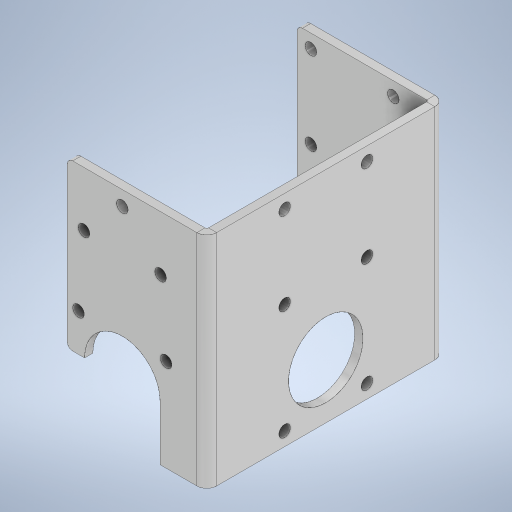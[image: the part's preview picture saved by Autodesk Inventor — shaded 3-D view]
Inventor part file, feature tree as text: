
AUTODESK INVENTOR PART (.ipt)
format: ipt  version: 2024.2 (Build 282272000, 272)  size: 324,096 bytes
history: native  units: in
note: dims shown in document units (in); Inventor stores cm internally (conversion verified against a paired STEP export)
features: reference x11, sketch x8, other x7, sheet_metal_op x4, hole x3, plane x1, chamfer x1, extrude x1
ambient origin geometry x8: Origin, YZ Plane, XZ Plane, XY Plane, X Axis, Y Axis, Z Axis, Center Point
bodies: Solid1 (feature_tree)
feature tree (36):
  sheet_metal_op  "Face1"
  sheet_metal_op  "Flange1"
  sketch  "Sketch3"  dims[d4=0.0295in d5=0.1181in]
  sketch  "Sketch4"  dims[d6=0.0122in d7=1.0039in d8=90.0deg d9=0.0122in]
  plane  "Work Plane1"
  hole  "Hole1"  [1 undecoded]
  sketch  "Sketch6"  dims[d11=0.0591in]
  chamfer  "Corner Round1"
  hole  "Hole3"  [1 undecoded]
  hole  "Hole4"  [1 undecoded]
  extrude  "Extrusion1"  Depth=1.0039in TaperAngle=90.0deg
  sketch  "Sketch1"  dims[d0=1.5787in d1=1.5945in]
  other  "Plate1"
  sketch  "Sketch2"  dims[d2=0.0591in d3=0.0591in]
  other  "Plate2"
  sheet_metal_op  "Bend1"
  sheet_metal_op  "Corner1"
  reference  "Reference1"
  sketch  "Sketch5"  dims[d10=0.2362in]
  reference  "Reference2"
  reference  "Reference3"
  reference  "Reference4"
  reference  "Reference5"
  reference  "Reference6"
  reference  "Reference7"
  reference  "Reference8"
  reference  "Reference9"
  reference  "Reference10"
  reference  "Reference11"
  sketch  "Sketch9"  dims[d12=0.0122in]
  sketch  "Sketch10"  dims[d13=0.0197in d14=0.0591in d15=0.0in d16=0.0591in d17=0.0in d18=0.0827in d19=0.2362in d20=0.1575in d21=0.0787in d22=90.0deg d23=0.0591in d24=0.0in d25=0.0394in d36=0.0827in d37=0.2362in d38=0.1575in d39=0.0787in d40=90.0deg d41=0.0591in d42=0.0in d43=0.0827in d44=0.2362in d45=0.1575in d46=0.0787in d47=90.0deg d48=0.0591in d49=0.8108in d50=0.0157in d51=0.0in d52=0.0in d53=0.1969in d54=0.0984in d55=0.0246in]
  other  "Cut1"
  other  "Cut2"
  other  "2_Arm.iam"
  other  "HTD-45H:3"
  other  "HTD-45H:1"
note: 3 required parameter values undecoded (feature->parameter linkage not recoverable at this tier; creation-order binding heuristic only, values carry confidence <= 0.55)
